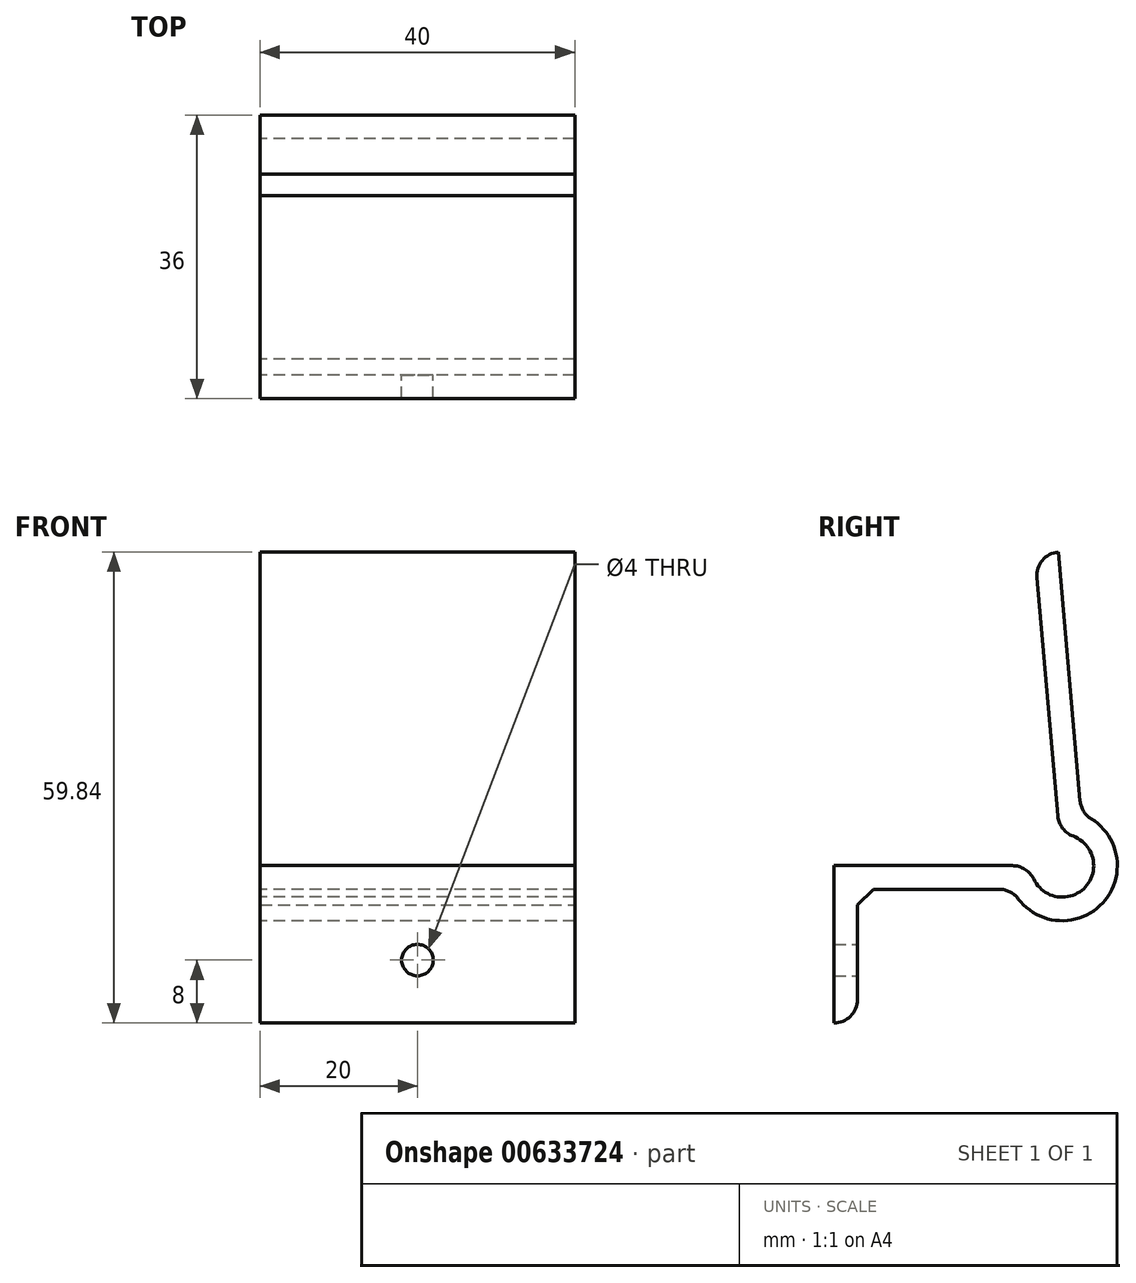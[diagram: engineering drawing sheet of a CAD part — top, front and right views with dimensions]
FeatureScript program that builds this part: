
annotation { "Feature Type Name" : "Feature", "Feature Type Description" : "" }
export const myFeature = defineFeature(function(context is Context, id is Id, definition is map)
    precondition{}
    {
        {
            var Q0;
            Q0=qCreatedBy(makeId("Right.planeOp"),FACE);
            var sketch = newSketch(context, id + "F0", { "sketchPlane" : qUnion([Q0])});
            skLineSegment(sketch, "E0", {"start": v(0, 0) * mm, "end": v(0, 20) * mm});
            skLineSegment(sketch, "E1", {"start": v(0, 20) * mm, "end": v(22.68, 20) * mm});
            skLineSegment(sketch, "E2", {"start": v(28.45, 26.3) * mm, "end": v(25.8, 56.59) * mm});
            skArc(sketch, "E3", {"start": v(25.39, 18.29) * mm, "mid": v(31.95, 17.3) * mm, "end": v(30.4, 23.75) * mm});
            skArc(sketch, "E4", {"start": v(23.4, 15.8) * mm, "mid": v(34.16, 15.27) * mm, "end": v(32.69, 25.95) * mm});
            skLineSegment(sketch, "E5", {"start": v(0, 0) * mm, "end": v(0, 0) * mm});
            skLineSegment(sketch, "E6", {"start": v(3, 3) * mm, "end": v(3, 17) * mm});
            skLineSegment(sketch, "E7", {"start": v(3, 17) * mm, "end": v(21, 17) * mm});
            skLineSegment(sketch, "E8", {"start": v(28.51, 59.85) * mm, "end": v(28.79, 59.85) * mm});
            skLineSegment(sketch, "E9", {"start": v(28.51, 59.85) * mm, "end": v(31.28, 28.24) * mm});
            skPoint(sketch, "E10.visualSharp", {"position": v(25.51, 59.85) * mm});
            skArc(sketch, "E10.filletArc", {"start": v(28.79, 59.85) * mm, "mid": v(26.58, 58.87) * mm, "end": v(25.8, 56.59) * mm});
            skPoint(sketch, "E11.visualSharp", {"position": v(3, 0) * mm});
            skArc(sketch, "E11.filletArc", {"start": v(0, 0) * mm, "mid": v(2.12, 0.88) * mm, "end": v(3, 3) * mm});
            skPoint(sketch, "E12.visualSharp", {"position": v(28.65, 23.98) * mm});
            skArc(sketch, "E12.filletArc", {"start": v(28.45, 26.3) * mm, "mid": v(29.05, 24.74) * mm, "end": v(30.4, 23.75) * mm});
            skPoint(sketch, "E13.visualSharp", {"position": v(25, 20) * mm});
            skArc(sketch, "E13.filletArc", {"start": v(25.39, 18.29) * mm, "mid": v(24.28, 19.54) * mm, "end": v(22.68, 20) * mm});
            skPoint(sketch, "E14.visualSharp", {"position": v(31.43, 26.57) * mm});
            skArc(sketch, "E14.filletArc", {"start": v(31.28, 28.24) * mm, "mid": v(31.71, 26.93) * mm, "end": v(32.69, 25.95) * mm});
            skArc(sketch, "E15.filletArc", {"start": v(23.4, 15.8) * mm, "mid": v(22.34, 16.68) * mm, "end": v(21, 17) * mm});
            skSolve(sketch);
        }
        {
            var Q0;
            Q0=makeQuery(id+"F0.imprint","IMPRINT",FACE,{"disambiguationData":[TD([[makeQuery(id+"F0.imprint","IMPRINT",EDGE,{"derivedFrom":sQuery(id+"F0.wireOp",EDGE,"E0")}),-1.0]])]});
            extrude(context, id + "F1", {"entities" : qUnion([Q0]), "depth" : 40 * mm, "offsetDistance" : 25 * mm});
        }
        {
            var Q0;
            Q0=makeQuery(id+"F1.opExtrude","SWEPT_FACE",FACE,{"disambiguationData":[OSD([sQuery(id+"F0.wireOp",EDGE,"E6")])]});
            var sketch = newSketch(context, id + "F2", { "sketchPlane" : qUnion([Q0])});
            skCircle(sketch, "E16", {"center": v(-20, 8) * mm, "radius": 2 * mm});
            skPoint(sketch, "E16.centerSnap0", {"position": v(-40, 10) * mm});
            skPoint(sketch, "E16.centerSnap1", {"position": v(-20, 3) * mm});
            skSolve(sketch);
        }
        {
            var Q0;
            Q0 = qSketchRegion(id + "F2", true);
            extrude(context, id + "F3", {"entities" : qUnion([Q0]), "operationType" : NewBodyOperationType.REMOVE, "oppositeDirection" : true, "depth" : 9.6 * mm, "offsetDistance" : 25 * mm});
        }
        {
            var Q0;
            Q0=makeQuery(id+"F1.opExtrude","SWEPT_EDGE",EDGE,{"disambiguationData":[OSD([sQuery(id+"F0.wireOp",EDGE,"E6"),sQuery(id+"F0.wireOp",EDGE,"E7")])]});
            chamfer(context, id + "F4", {"entities" : qUnion([Q0]), "width" : 2 * mm, "tangentPropagation" : true});
        }
    });
